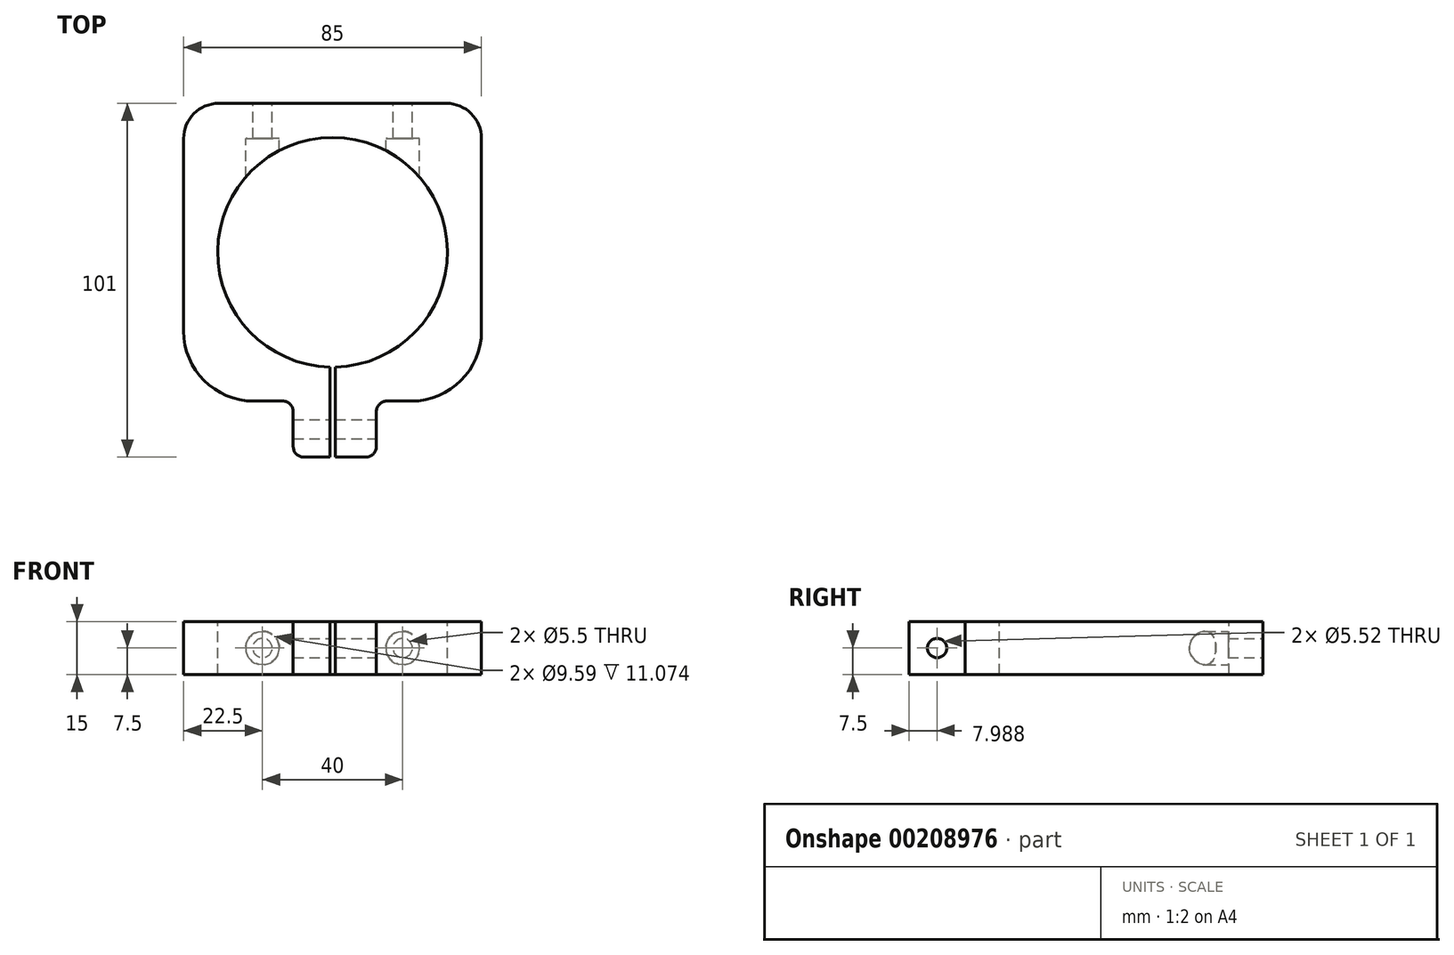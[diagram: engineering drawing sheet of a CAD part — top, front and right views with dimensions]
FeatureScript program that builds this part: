
annotation { "Feature Type Name" : "Feature", "Feature Type Description" : "" }
export const myFeature = defineFeature(function(context is Context, id is Id, definition is map)
    precondition{}
    {
        {
            var Q0;
            Q0=qCreatedBy(makeId("Top.planeOp"),FACE);
            var sketch = newSketch(context, id + "F0", { "sketchPlane" : qUnion([Q0])});
            skLineSegment(sketch, "E0", {"start": v(-32.5, 42.5) * mm, "end": v(0, 42.5) * mm});
            skLineSegment(sketch, "E1", {"start": v(0, 42.5) * mm, "end": v(32.5, 42.5) * mm});
            skLineSegment(sketch, "E2", {"start": v(42.5, 32.5) * mm, "end": v(42.5, 0) * mm});
            skLineSegment(sketch, "E3", {"start": v(42.5, 0) * mm, "end": v(42.5, -22.5) * mm});
            skLineSegment(sketch, "E4", {"start": v(22.5, -42.5) * mm, "end": v(15.5, -42.5) * mm});
            skLineSegment(sketch, "E5", {"start": v(12.5, -45.5) * mm, "end": v(12.5, -55.5) * mm});
            skLineSegment(sketch, "E6", {"start": v(9.5, -58.5) * mm, "end": v(-8.22, -58.5) * mm});
            skLineSegment(sketch, "E7", {"start": v(-11.22, -55.5) * mm, "end": v(-11.22, -45.5) * mm});
            skLineSegment(sketch, "E8", {"start": v(-14.22, -42.5) * mm, "end": v(-22.5, -42.5) * mm});
            skLineSegment(sketch, "E9", {"start": v(-42.5, -22.5) * mm, "end": v(-42.5, 0) * mm});
            skLineSegment(sketch, "E10", {"start": v(-42.5, 0) * mm, "end": v(-42.5, 32.5) * mm});
            skLineSegment(sketch, "E11", {"start": v(-42.5, 0) * mm, "end": v(0, 0) * mm, "construction": true});
            skLineSegment(sketch, "E12", {"start": v(0, 0) * mm, "end": v(42.5, 0) * mm, "construction": true});
            skPoint(sketch, "E13.visualSharp", {"position": v(-42.5, 42.5) * mm});
            skArc(sketch, "E13.filletArc", {"start": v(-32.5, 42.5) * mm, "mid": v(-39.57, 39.57) * mm, "end": v(-42.5, 32.5) * mm});
            skPoint(sketch, "E14.visualSharp", {"position": v(42.5, 42.5) * mm});
            skArc(sketch, "E14.filletArc", {"start": v(42.5, 32.5) * mm, "mid": v(39.57, 39.57) * mm, "end": v(32.5, 42.5) * mm});
            skPoint(sketch, "E15.visualSharp", {"position": v(-42.5, -42.5) * mm});
            skArc(sketch, "E15.filletArc", {"start": v(-42.5, -22.5) * mm, "mid": v(-36.64, -36.64) * mm, "end": v(-22.5, -42.5) * mm});
            skPoint(sketch, "E16.visualSharp", {"position": v(-11.22, -42.5) * mm});
            skArc(sketch, "E16.filletArc", {"start": v(-11.22, -45.5) * mm, "mid": v(-12.1, -43.38) * mm, "end": v(-14.22, -42.5) * mm});
            skPoint(sketch, "E17.visualSharp", {"position": v(12.5, -42.5) * mm});
            skArc(sketch, "E17.filletArc", {"start": v(15.5, -42.5) * mm, "mid": v(13.38, -43.38) * mm, "end": v(12.5, -45.5) * mm});
            skPoint(sketch, "E18.visualSharp", {"position": v(12.5, -58.5) * mm});
            skArc(sketch, "E18.filletArc", {"start": v(9.5, -58.5) * mm, "mid": v(11.62, -57.62) * mm, "end": v(12.5, -55.5) * mm});
            skPoint(sketch, "E19.visualSharp", {"position": v(-11.22, -58.5) * mm});
            skArc(sketch, "E19.filletArc", {"start": v(-11.22, -55.5) * mm, "mid": v(-10.34, -57.62) * mm, "end": v(-8.22, -58.5) * mm});
            skPoint(sketch, "E20.visualSharp", {"position": v(42.5, -42.5) * mm});
            skArc(sketch, "E20.filletArc", {"start": v(22.5, -42.5) * mm, "mid": v(36.64, -36.64) * mm, "end": v(42.5, -22.5) * mm});
            skSolve(sketch);
        }
        {
            var Q0;
            Q0=qSketchRegion(id+"F0",true);
            extrude(context, id + "F1", {"entities" : qUnion([Q0]), "endBound" : BoundingType.SYMMETRIC, "depth" : 15 * mm});
        }
        {
            var Q0;
            Q0=qCreatedBy(makeId("Top.planeOp"),FACE);
            var sketch = newSketch(context, id + "F2", { "sketchPlane" : qUnion([Q0])});
            skCircle(sketch, "E21", {"center": v(0, 0) * mm, "radius": 32.77 * mm});
            skSolve(sketch);
        }
        {
            var Q0;
            Q0=qSketchRegion(id+"F2",true);
            extrude(context, id + "F3", {"entities" : qUnion([Q0]), "operationType" : NewBodyOperationType.REMOVE, "endBound" : BoundingType.SYMMETRIC, "oppositeDirection" : true, "depth" : 16 * mm});
        }
        {
            var Q0;
            Q0=qCreatedBy(makeId("Top.planeOp"),FACE);
            var sketch = newSketch(context, id + "F4", { "sketchPlane" : qUnion([Q0])});
            skLineSegment(sketch, "E22.bottom", {"start": v(0, 0) * mm, "end": v(0.75, 0) * mm});
            skLineSegment(sketch, "E22.top", {"start": v(0, -80) * mm, "end": v(0.75, -80) * mm});
            skLineSegment(sketch, "E22.left", {"start": v(0, 0) * mm, "end": v(0, -80) * mm});
            skLineSegment(sketch, "E22.right", {"start": v(0.75, 0) * mm, "end": v(0.75, -80) * mm});
            skLineSegment(sketch, "E23.bottom", {"start": v(0, 0) * mm, "end": v(-0.75, 0) * mm});
            skLineSegment(sketch, "E23.top", {"start": v(0, -80) * mm, "end": v(-0.75, -80) * mm});
            skLineSegment(sketch, "E23.right", {"start": v(-0.75, 0) * mm, "end": v(-0.75, -80) * mm});
            skSolve(sketch);
        }
        {
            var Q0;
            Q0=qSketchRegion(id+"F4",true);
            extrude(context, id + "F5", {"entities" : qUnion([Q0]), "operationType" : NewBodyOperationType.REMOVE, "endBound" : BoundingType.SYMMETRIC, "oppositeDirection" : true, "depth" : 15 * mm});
        }
        {
            var Q0;
            Q0=qCreatedBy(makeId("Right.planeOp"),FACE);
            var sketch = newSketch(context, id + "F6", { "sketchPlane" : qUnion([Q0])});
            skLineSegment(sketch, "E24", {"start": v(-45.5, 0) * mm, "end": v(-50.51, 0) * mm, "construction": true});
            skLineSegment(sketch, "E25", {"start": v(-50.51, 0) * mm, "end": v(-55.52, 0) * mm, "construction": true});
            skLineSegment(sketch, "E26", {"start": v(-50.51, 0) * mm, "end": v(-50.51, -7.5) * mm, "construction": true});
            skLineSegment(sketch, "E27", {"start": v(-50.51, 0) * mm, "end": v(-50.51, 7.5) * mm, "construction": true});
            skCircle(sketch, "E28", {"center": v(-50.51, 0) * mm, "radius": 2.76 * mm});
            skSolve(sketch);
        }
        {
            var Q0;
            Q0=qSketchRegion(id+"F6",true);
            extrude(context, id + "F7", {"entities" : qUnion([Q0]), "operationType" : NewBodyOperationType.REMOVE, "endBound" : BoundingType.SYMMETRIC, "oppositeDirection" : true, "depth" : 50 * mm});
        }
        {
            var Q0;
            Q0=makeQuery(id+"F1.opExtrude","SWEPT_FACE",FACE,{"disambiguationData":[OSD([sQuery(id+"F0.wireOp",EDGE,"E0"),sQuery(id+"F0.wireOp",EDGE,"E1")])]});
            var sketch = newSketch(context, id + "F8", { "sketchPlane" : qUnion([Q0])});
            skLineSegment(sketch, "E29", {"start": v(0, 0) * mm, "end": v(20, 0) * mm, "construction": true});
            skLineSegment(sketch, "E30", {"start": v(0, 0) * mm, "end": v(-20, 0) * mm, "construction": true});
            skCircle(sketch, "E31", {"center": v(20, 0) * mm, "radius": 2.75 * mm});
            skCircle(sketch, "E32", {"center": v(-20, 0) * mm, "radius": 2.75 * mm});
            skSolve(sketch);
        }
        {
            var Q0;
            Q0=qSketchRegion(id+"F8",true);
            extrude(context, id + "F9", {"entities" : qUnion([Q0]), "operationType" : NewBodyOperationType.REMOVE, "oppositeDirection" : true, "depth" : 25 * mm});
        }
        {
            var Q0;
            Q0=makeQuery(id+"F1.opExtrude","SWEPT_FACE",FACE,{"disambiguationData":[OSD([sQuery(id+"F0.wireOp",EDGE,"E0"),sQuery(id+"F0.wireOp",EDGE,"E1")])]});
            var sketch = newSketch(context, id + "F10", { "sketchPlane" : qUnion([Q0])});
            skCircle(sketch, "E33", {"center": v(20, 0) * mm, "radius": 4.8 * mm});
            skCircle(sketch, "E34", {"center": v(-20, 0) * mm, "radius": 4.8 * mm});
            skSolve(sketch);
        }
        {
            var Q0;
            Q0=qSketchRegion(id+"F10",true);
            extrude(context, id + "F11", {"entities" : qUnion([Q0]), "operationType" : NewBodyOperationType.REMOVE, "oppositeDirection" : true, "depth" : 22 * mm, "hasSecondDirection" : true, "secondDirectionOppositeDirection" : true, "secondDirectionDepth" : 10 * mm});
        }
    });
